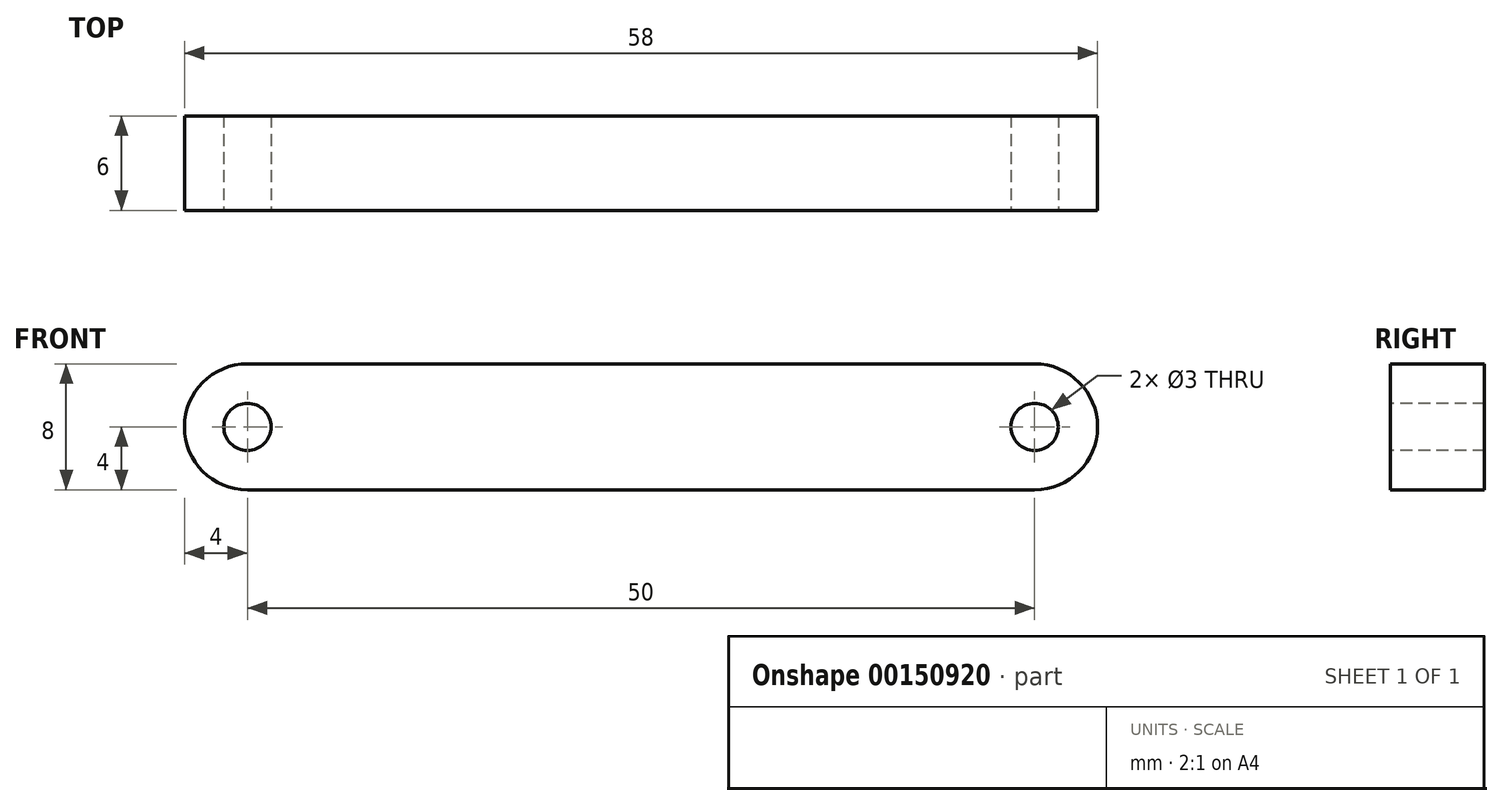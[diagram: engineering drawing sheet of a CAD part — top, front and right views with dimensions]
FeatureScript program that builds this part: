
annotation { "Feature Type Name" : "Feature", "Feature Type Description" : "" }
export const myFeature = defineFeature(function(context is Context, id is Id, definition is map)
    precondition{}
    {
        {
            var Q0;
            Q0=qCreatedBy(makeId("Front.planeOp"),FACE);
            var sketch = newSketch(context, id + "F0", { "sketchPlane" : qUnion([Q0])});
            skLineSegment(sketch, "E0.bottom", {"start": v(0, 0) * mm, "end": v(50, 0) * mm});
            skLineSegment(sketch, "E0.top", {"start": v(0, 8) * mm, "end": v(50, 8) * mm});
            skArc(sketch, "E1", {"start": v(0, 8) * mm, "mid": v(-4, 4) * mm, "end": v(0, 0) * mm});
            skArc(sketch, "E2", {"start": v(50, 0) * mm, "mid": v(54, 4) * mm, "end": v(50, 8) * mm});
            skSolve(sketch);
        }
        {
            var Q0;
            Q0 = qSketchRegion(id + "F0", true);
            extrude(context, id + "F1", {"entities" : qUnion([Q0]), "depth" : 6 * mm});
        }
        {
            var Q0;
            Q0=makeQuery(id+"F1.opExtrude","CAP_FACE",FACE,{"disambiguationData":[OSD([sQuery(id+"F0.wireOp",EDGE,"E0.bottom"),sQuery(id+"F0.wireOp",EDGE,"E0.top"),sQuery(id+"F0.wireOp",EDGE,"HIoaqUXj-zCnZ-PLay-zYgn-YaQb4ij7V86C"),sQuery(id+"F0.wireOp",EDGE,"LPRup51T-Z1iP-anKY-cxDH-ksB0blUbg6ey")])],"isStart":false});
            var sketch = newSketch(context, id + "F2", { "sketchPlane" : qUnion([Q0])});
            skCircle(sketch, "E3", {"center": v(0, 4) * mm, "radius": 1.5 * mm});
            skSolve(sketch);
        }
        {
            var Q0;
            Q0 = qSketchRegion(id + "F2", true);
            extrude(context, id + "F3", {"entities" : qUnion([Q0]), "operationType" : NewBodyOperationType.REMOVE, "endBound" : BoundingType.THROUGH_ALL, "oppositeDirection" : true, "depth" : 25 * mm});
        }
        {
            var Q0;
            Q0=makeQuery(id+"F1.opExtrude","CAP_FACE",FACE,{"disambiguationData":[OSD([sQuery(id+"F0.wireOp",EDGE,"E0.bottom"),sQuery(id+"F0.wireOp",EDGE,"E0.top"),sQuery(id+"F0.wireOp",EDGE,"HIoaqUXj-zCnZ-PLay-zYgn-YaQb4ij7V86C"),sQuery(id+"F0.wireOp",EDGE,"LPRup51T-Z1iP-anKY-cxDH-ksB0blUbg6ey")])],"isStart":false});
            var sketch = newSketch(context, id + "F4", { "sketchPlane" : qUnion([Q0])});
            skCircle(sketch, "E4", {"center": v(50, 4) * mm, "radius": 1.5 * mm});
            skSolve(sketch);
        }
        {
            var Q0;
            Q0 = qSketchRegion(id + "F4", true);
            extrude(context, id + "F5", {"entities" : qUnion([Q0]), "operationType" : NewBodyOperationType.REMOVE, "endBound" : BoundingType.THROUGH_ALL, "oppositeDirection" : true, "depth" : 25 * mm});
        }
    });
